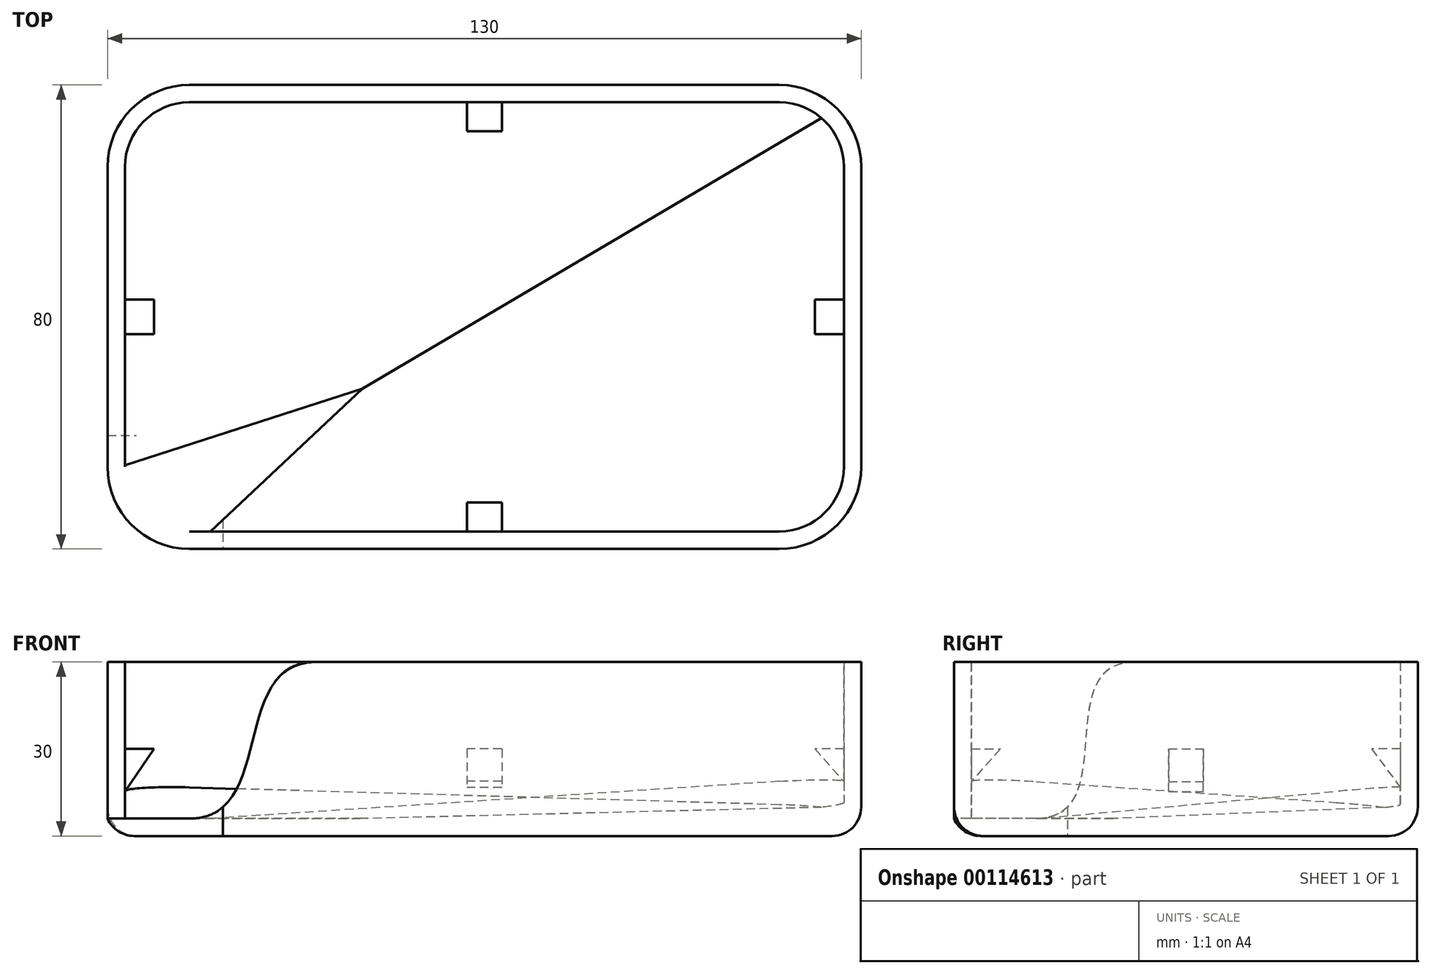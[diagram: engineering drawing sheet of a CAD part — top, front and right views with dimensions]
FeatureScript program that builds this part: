
annotation { "Feature Type Name" : "Feature", "Feature Type Description" : "" }
export const myFeature = defineFeature(function(context is Context, id is Id, definition is map)
    precondition{}
    {
        {
            var Q0;
            Q0=qCreatedBy(makeId("Top.planeOp"),FACE);
            var sketch = newSketch(context, id + "F0", { "sketchPlane" : qUnion([Q0])});
            skLineSegment(sketch, "E0.bottom", {"start": v(65, -40) * mm, "end": v(50.86, -40) * mm, "construction": true});
            skLineSegment(sketch, "E0.top", {"start": v(65, 40) * mm, "end": v(50.86, 40) * mm, "construction": true});
            skLineSegment(sketch, "E0.left", {"start": v(65, -40) * mm, "end": v(65, -25.86) * mm, "construction": true});
            skLineSegment(sketch, "E0.right", {"start": v(-65, -40) * mm, "end": v(-65, -25.86) * mm, "construction": true});
            skPoint(sketch, "E0.middle", {"position": v(0, 0) * mm});
            skArc(sketch, "E1", {"start": v(-50.86, 40) * mm, "mid": v(-60.86, 35.86) * mm, "end": v(-65, 25.86) * mm});
            skArc(sketch, "E2", {"start": v(-65, -25.86) * mm, "mid": v(-60.86, -35.86) * mm, "end": v(-50.86, -40) * mm});
            skArc(sketch, "E3", {"start": v(65, 25.86) * mm, "mid": v(60.86, 35.86) * mm, "end": v(50.86, 40) * mm});
            skArc(sketch, "E4", {"start": v(50.86, -40) * mm, "mid": v(60.86, -35.86) * mm, "end": v(65, -25.86) * mm});
            skLineSegment(sketch, "E5", {"start": v(65, 40) * mm, "end": v(50.86, 25.86) * mm, "construction": true});
            skLineSegment(sketch, "E6", {"start": v(-65, 40) * mm, "end": v(-50.86, 25.86) * mm, "construction": true});
            skLineSegment(sketch, "E7", {"start": v(-50.86, -25.86) * mm, "end": v(-65, -40) * mm, "construction": true});
            skLineSegment(sketch, "E8", {"start": v(50.86, -25.86) * mm, "end": v(65, -40) * mm, "construction": true});
            skLineSegment(sketch, "E9", {"start": v(-50.86, 40) * mm, "end": v(-65, 40) * mm, "construction": true});
            skLineSegment(sketch, "E10", {"start": v(-65, 25.86) * mm, "end": v(-65, 40) * mm, "construction": true});
            skLineSegment(sketch, "E11", {"start": v(-65, -25.86) * mm, "end": v(-65, 25.86) * mm});
            skLineSegment(sketch, "E12", {"start": v(-50.86, -40) * mm, "end": v(-65, -40) * mm, "construction": true});
            skLineSegment(sketch, "E13", {"start": v(50.86, -40) * mm, "end": v(-50.86, -40) * mm});
            skLineSegment(sketch, "E14", {"start": v(65, -25.86) * mm, "end": v(65, 25.86) * mm});
            skLineSegment(sketch, "E15", {"start": v(65, 25.86) * mm, "end": v(65, 40) * mm, "construction": true});
            skLineSegment(sketch, "E16", {"start": v(50.86, 40) * mm, "end": v(-50.86, 40) * mm});
            skLineSegment(sketch, "E17", {"start": v(-60.86, 35.86) * mm, "end": v(60.86, -35.86) * mm, "construction": true});
            skLineSegment(sketch, "E18", {"start": v(60.86, 35.86) * mm, "end": v(-60.86, -35.86) * mm, "construction": true});
            skLineSegment(sketch, "E19", {"start": v(39.73, 71.72) * mm, "end": v(81.99, 0) * mm, "construction": true});
            skLineSegment(sketch, "E20", {"start": v(-65, -25.86) * mm, "end": v(-50.86, -40) * mm, "construction": true});
            skSolve(sketch);
        }
        {
            var Q0;
            Q0 = qSketchRegion(id + "F0", true);
            extrude(context, id + "F1", {"entities" : qUnion([Q0]), "depth" : 30 * mm});
        }
        {
            var Q0;
            Q0=makeQuery(id+"F1.opExtrude","CAP_FACE",FACE,{"disambiguationData":[OSD([sQuery(id+"F0.wireOp",EDGE,"E1"),sQuery(id+"F0.wireOp",EDGE,"E2"),sQuery(id+"F0.wireOp",EDGE,"E3"),sQuery(id+"F0.wireOp",EDGE,"E4"),sQuery(id+"F0.wireOp",EDGE,"E11"),sQuery(id+"F0.wireOp",EDGE,"E13"),sQuery(id+"F0.wireOp",EDGE,"E14"),sQuery(id+"F0.wireOp",EDGE,"E16")])],"isStart":false});
            shell(context, id + "F2", {"entities" : qUnion([Q0]), "thickness" : 3 * mm});
        }
        {
            var Q0;
            Q0=sQuery(id+"F0.wireOp",EDGE,"E19");
            cPlane(context, id + "F3", {"entities" : qUnion([Q0]), "cplaneType" : CPlaneType.LINE_ANGLE, "offset" : 25 * mm, "angle" : 90 * degree, "width" : 150 * mm, "height" : 150 * mm});
        }
        {
            var Q0;
            Q0=qCreatedBy(id+"F3.planeOp",FACE);
            var sketch = newSketch(context, id + "F4", { "sketchPlane" : qUnion([Q0])});
            skLineSegment(sketch, "E21.0", {"start": v(-10.72, 0) * mm, "end": v(8.65, 0) * mm, "construction": true});
            skLineSegment(sketch, "E22", {"start": v(0, 0) * mm, "end": v(75, 0) * mm});
            skPoint(sketch, "E22.endSnap0", {"position": v(-1.04, 0) * mm});
            skLineSegment(sketch, "E23", {"start": v(75, 0) * mm, "end": v(75, 12) * mm});
            skLineSegment(sketch, "E24", {"start": v(0, 0) * mm, "end": v(0, 5) * mm, "construction": true});
            skLineSegment(sketch, "E25", {"start": v(75, 12) * mm, "end": v(0, 5) * mm});
            skLineSegment(sketch, "E26.MirrorCS", {"start": v(0, 0) * mm, "end": v(-75, 0) * mm});
            skLineSegment(sketch, "E27.MirrorCS", {"start": v(-75, 0) * mm, "end": v(-75, 12) * mm});
            skLineSegment(sketch, "E28.MirrorCS", {"start": v(-75, 12) * mm, "end": v(0, 5) * mm});
            skSolve(sketch);
        }
        {
            var Q0;
            Q0 = qSketchRegion(id + "F4", true);
            extrude(context, id + "F5", {"entities" : qUnion([Q0]), "operationType" : NewBodyOperationType.ADD, "oppositeDirection" : true, "depth" : 140 * mm, "hasDraft" : true, "draftAngle" : 1.2 * degree, "draftPullDirection" : true});
        }
        {
            var Q0;
            Q0=qCreatedBy(makeId("Top.planeOp"),FACE);
            var sketch = newSketch(context, id + "F6", { "sketchPlane" : qUnion([Q0])});
            skArc(sketch, "E29.0", {"start": v(-50.86, 40) * mm, "mid": v(-60.86, 35.86) * mm, "end": v(-65, 25.86) * mm});
            skLineSegment(sketch, "E29.1", {"start": v(-65, -25.86) * mm, "end": v(-65, 25.86) * mm});
            skArc(sketch, "E29.2", {"start": v(-65, -25.86) * mm, "mid": v(-60.86, -35.86) * mm, "end": v(-50.86, -40) * mm});
            skLineSegment(sketch, "E29.3", {"start": v(50.86, -40) * mm, "end": v(-50.86, -40) * mm});
            skArc(sketch, "E29.4", {"start": v(50.86, -40) * mm, "mid": v(60.86, -35.86) * mm, "end": v(65, -25.86) * mm});
            skLineSegment(sketch, "E29.5", {"start": v(65, -25.86) * mm, "end": v(65, 25.86) * mm});
            skArc(sketch, "E29.6", {"start": v(65, 25.86) * mm, "mid": v(60.86, 35.86) * mm, "end": v(50.86, 40) * mm});
            skLineSegment(sketch, "E29.7", {"start": v(50.86, 40) * mm, "end": v(-50.86, 40) * mm});
            skLineSegment(sketch, "E30", {"start": v(-101.68, 119.74) * mm, "end": v(120.2, 119.74) * mm});
            skLineSegment(sketch, "E31", {"start": v(120.2, 119.74) * mm, "end": v(120.2, -100.68) * mm});
            skLineSegment(sketch, "E32", {"start": v(120.2, -100.68) * mm, "end": v(-101.68, -100.68) * mm});
            skLineSegment(sketch, "E33", {"start": v(-101.68, -100.68) * mm, "end": v(-101.68, 119.74) * mm});
            skSolve(sketch);
        }
        {
            var Q0;
            Q0 = qSketchRegion(id + "F6", true);
            extrude(context, id + "F7", {"entities" : qUnion([Q0]), "operationType" : NewBodyOperationType.REMOVE, "depth" : 25 * mm});
        }
        {
            var Q0;
            {var subQ2=sQuery(id+"F0.wireOp",EDGE,"E13");var subQ10=makeQuery(id+"F1.opExtrude","SWEPT_FACE",FACE,{"disambiguationData":[OSD([subQ2])]});Q0=makeQuery(id+"F7.boolean.opBoolean","MERGE",FACE,{"derivedFrom":[makeQuery(id+"F5.boolean.opBoolean","SPLIT",FACE,{"disambiguationData":[TD([makeQuery(id+"F5.opExtrude","SWEPT_FACE",FACE,{"disambiguationData":[OSD([sQuery(id+"F4.wireOp",EDGE,"E22"),sQuery(id+"F4.wireOp",EDGE,"E26.MirrorCS")])]})])],"derivedFrom":subQ10}),makeQuery(id+"F5.boolean.opBoolean","SPLIT",FACE,{"disambiguationData":[TD([makeQuery(id+"F5.opExtrude","SWEPT_FACE",FACE,{"disambiguationData":[OSD([sQuery(id+"F4.wireOp",EDGE,"E28.MirrorCS")])]})])],"derivedFrom":subQ10}),makeQuery(id+"F7.opExtrude","SWEPT_FACE",FACE,{"disambiguationData":[OSD([sQuery(id+"F6.wireOp",EDGE,"E29.3")])]})]});}
            var sketch = newSketch(context, id + "F8", { "sketchPlane" : qUnion([Q0])});
            skLineSegment(sketch, "E34.0", {"start": v(-47.23, 3) * mm, "end": v(-50.86, 3) * mm, "construction": true});
            skFitSpline(sketch, "E35", {"points": [v(-50.86, 3) * mm, v(-29.05, 30) * mm], "startDerivative": vector(45, 0) * mm, "endDerivative": vector(45, 0) * mm});
            skLineSegment(sketch, "E36", {"start": v(-35.86, 3) * mm, "end": v(-50.86, 3) * mm, "construction": true});
            skLineSegment(sketch, "E37", {"start": v(-29.05, 30) * mm, "end": v(-44.05, 30) * mm, "construction": true});
            skLineSegment(sketch, "E38.0", {"start": v(50.86, 30) * mm, "end": v(-50.86, 30) * mm});
            skLineSegment(sketch, "E39", {"start": v(-50.86, 30) * mm, "end": v(-50.86, 3) * mm});
            skSolve(sketch);
        }
        {
            var Q0;
            Q0 = qSketchRegion(id + "F8", true);
            var Q1;
            Q1=makeQuery(id+"F2.opShell","OFFSET_FACE",FACE,{"disambiguationData":[OSD([sQuery(id+"F0.wireOp",EDGE,"E13")])]});
            extrude(context, id + "F9", {"entities" : qUnion([Q0]), "operationType" : NewBodyOperationType.REMOVE, "endBound" : BoundingType.UP_TO_SURFACE, "oppositeDirection" : true, "endBoundEntityFace" : qUnion([Q1]), "depth" : 25 * mm});
        }
        {
            var Q0;
            {var subQ5=sQuery(id+"F0.wireOp",EDGE,"E11");var subQ10=makeQuery(id+"F1.opExtrude","SWEPT_FACE",FACE,{"disambiguationData":[OSD([subQ5])]});Q0=makeQuery(id+"F7.boolean.opBoolean","MERGE",FACE,{"derivedFrom":[makeQuery(id+"F5.boolean.opBoolean","SPLIT",FACE,{"disambiguationData":[TD([makeQuery(id+"F5.opExtrude","SWEPT_FACE",FACE,{"disambiguationData":[OSD([sQuery(id+"F4.wireOp",EDGE,"E22"),sQuery(id+"F4.wireOp",EDGE,"E26.MirrorCS")])]})])],"derivedFrom":subQ10}),makeQuery(id+"F5.boolean.opBoolean","SPLIT",FACE,{"disambiguationData":[TD([makeQuery(id+"F5.opExtrude","SWEPT_FACE",FACE,{"disambiguationData":[OSD([sQuery(id+"F4.wireOp",EDGE,"E25")])]})])],"derivedFrom":subQ10}),makeQuery(id+"F7.opExtrude","SWEPT_FACE",FACE,{"disambiguationData":[OSD([sQuery(id+"F6.wireOp",EDGE,"E29.1")])]})]});}
            var sketch = newSketch(context, id + "F10", { "sketchPlane" : qUnion([Q0])});
            skLineSegment(sketch, "E40.0", {"start": v(25.86, 3) * mm, "end": v(25.55, 3) * mm, "construction": true});
            skLineSegment(sketch, "E41.0", {"start": v(25.86, 30) * mm, "end": v(-25.86, 30) * mm});
            skFitSpline(sketch, "E42", {"points": [v(8.75, 30) * mm, v(25.86, 3) * mm], "startDerivative": vector(45, 0) * mm, "endDerivative": vector(45, 0) * mm});
            skLineSegment(sketch, "E43", {"start": v(8.75, 30) * mm, "end": v(23.75, 30) * mm, "construction": true});
            skLineSegment(sketch, "E44", {"start": v(25.86, 3) * mm, "end": v(10.86, 3) * mm, "construction": true});
            skLineSegment(sketch, "E45", {"start": v(25.86, 30) * mm, "end": v(25.86, 3) * mm});
            skSolve(sketch);
        }
        {
            var Q0;
            Q0 = qSketchRegion(id + "F10", true);
            var Q1;
            Q1=makeQuery(id+"F2.opShell","OFFSET_FACE",FACE,{"disambiguationData":[OSD([sQuery(id+"F0.wireOp",EDGE,"E11")])]});
            extrude(context, id + "F11", {"entities" : qUnion([Q0]), "operationType" : NewBodyOperationType.REMOVE, "endBound" : BoundingType.UP_TO_SURFACE, "oppositeDirection" : true, "endBoundEntityFace" : qUnion([Q1]), "depth" : 25 * mm});
        }
        {
            var Q0;
            Q0=makeQuery(id+"F2.opShell","OFFSET_FACE",FACE,{"disambiguationData":[OSD([sQuery(id+"F0.wireOp",EDGE,"E1"),sQuery(id+"F0.wireOp",EDGE,"E2"),sQuery(id+"F0.wireOp",EDGE,"E3"),sQuery(id+"F0.wireOp",EDGE,"E4"),sQuery(id+"F0.wireOp",EDGE,"E11"),sQuery(id+"F0.wireOp",EDGE,"E13"),sQuery(id+"F0.wireOp",EDGE,"E14"),sQuery(id+"F0.wireOp",EDGE,"E16")])]});
            var sketch = newSketch(context, id + "F12", { "sketchPlane" : qUnion([Q0])});
            skArc(sketch, "E46.0", {"start": v(-65, -25.86) * mm, "mid": v(-60.86, -35.86) * mm, "end": v(-50.86, -40) * mm});
            skArc(sketch, "E46.1", {"start": v(-62, -25.86) * mm, "mid": v(-58.74, -33.74) * mm, "end": v(-50.86, -37) * mm});
            skLineSegment(sketch, "E46.2", {"start": v(-62, -25.86) * mm, "end": v(-65, -25.86) * mm});
            skLineSegment(sketch, "E46.3", {"start": v(-50.86, -37) * mm, "end": v(-50.86, -40) * mm});
            skSolve(sketch);
        }
        {
            var Q0;
            Q0 = qSketchRegion(id + "F12", true);
            var Q1;
            {var subQ0=sQuery(id+"F0.wireOp",EDGE,"E14");var subQ1=sQuery(id+"F0.wireOp",EDGE,"E11");var subQ2=sQuery(id+"F0.wireOp",EDGE,"E3");var subQ3=sQuery(id+"F0.wireOp",EDGE,"E16");var subQ4=sQuery(id+"F0.wireOp",EDGE,"E4");var subQ5=sQuery(id+"F0.wireOp",EDGE,"E13");var subQ6=sQuery(id+"F0.wireOp",EDGE,"E1");Q1=makeQuery(id+"F11.boolean.opBoolean","SPLIT",FACE,{"disambiguationData":[TD([makeQuery(id+"F1.opExtrude","SWEPT_FACE",FACE,{"disambiguationData":[OSD([subQ6])]})])],"derivedFrom":makeQuery(id+"F1.opExtrude","CAP_FACE",FACE,{"disambiguationData":[OSD([subQ6,sQuery(id+"F0.wireOp",EDGE,"E2"),subQ2,subQ4,subQ1,subQ5,subQ0,subQ3])],"isStart":false})});}
            extrude(context, id + "F13", {"entities" : qUnion([Q0]), "operationType" : NewBodyOperationType.REMOVE, "endBound" : BoundingType.UP_TO_SURFACE, "endBoundEntityFace" : qUnion([Q1]), "depth" : 25 * mm});
        }
        {
            var Q0;
            Q0=makeQuery(id+"F1.opExtrude","CAP_FACE",FACE,{"disambiguationData":[OSD([sQuery(id+"F0.wireOp",EDGE,"E1"),sQuery(id+"F0.wireOp",EDGE,"E2"),sQuery(id+"F0.wireOp",EDGE,"E3"),sQuery(id+"F0.wireOp",EDGE,"E4"),sQuery(id+"F0.wireOp",EDGE,"E11"),sQuery(id+"F0.wireOp",EDGE,"E13"),sQuery(id+"F0.wireOp",EDGE,"E14"),sQuery(id+"F0.wireOp",EDGE,"E16")])],"isStart":true});
            fillet(context, id + "F14", {"entities" : qUnion([Q0]), "radius" : 5 * mm, "tangentPropagation" : true, "allowEdgeOverflow" : false});
        }
        {
            var Q0;
            Q0=qCreatedBy(makeId("Front.planeOp"),FACE);
            var sketch = newSketch(context, id + "F15", { "sketchPlane" : qUnion([Q0])});
            skFitSpline(sketch, "E47.0", {"points": [v(-62, 3.12) * mm, v(-62, 12.08) * mm, v(-62, 21.04) * mm, v(-62, 30) * mm]});
            skLineSegment(sketch, "E48.0", {"start": v(62, 30) * mm, "end": v(62, 9.38) * mm});
            skLineSegment(sketch, "E49", {"start": v(-62, 30) * mm, "end": v(-62, 0) * mm, "construction": true});
            skLineSegment(sketch, "E50", {"start": v(62, 30) * mm, "end": v(62, 0) * mm, "construction": true});
            skLineSegment(sketch, "E51", {"start": v(-62, 15) * mm, "end": v(-57, 15) * mm});
            skLineSegment(sketch, "E52", {"start": v(62, 15) * mm, "end": v(57, 15) * mm});
            skPoint(sketch, "E52.endSnap0", {"position": v(62, 15) * mm});
            skEllipticalArc(sketch, "E53.0", {});
            skEllipticalArc(sketch, "E54.0", {});
            skLineSegment(sketch, "E55", {"start": v(-57, 15) * mm, "end": v(-62, 7.68) * mm});
            skLineSegment(sketch, "E56", {"start": v(57, 15) * mm, "end": v(62, 9.38) * mm});
            const initialGuessF15  = {"E53.0": [-0.050857864376269046, 0.0073572243298795775, 0.9995651955649583, -0.029485925713581156, 0.011146942206523262, 0.0010145309923370737, 1.5734811282030245, 3.1442774549979204], "E54.0": [0.050857864376269046, 0.008648581469915026, -0.9978405935118139, -0.0656821889098638, 0.011166131468866098, 0.00077530749382443, 3.137022248751718, 4.707818575546617]};
            skSetInitialGuess(sketch, initialGuessF15);
            skSolve(sketch);
        }
        {
            var Q0;
            Q0 = qSketchRegion(id + "F15", true);
            extrude(context, id + "F16", {"entities" : qUnion([Q0]), "operationType" : NewBodyOperationType.ADD, "depth" : 6 * mm, "symmetric" : true});
        }
        {
            var Q0;
            Q0=qCreatedBy(makeId("Right.planeOp"),FACE);
            var sketch = newSketch(context, id + "F17", { "sketchPlane" : qUnion([Q0])});
            skLineSegment(sketch, "E57.0", {"start": v(-37, 30) * mm, "end": v(-37, 9.43) * mm});
            skLineSegment(sketch, "E58.0", {"start": v(37, 30) * mm, "end": v(37, 5.4) * mm});
            skEllipticalArc(sketch, "E59.0", {});
            skEllipticalArc(sketch, "E60.0", {});
            skLineSegment(sketch, "E61", {"start": v(-37, 30) * mm, "end": v(-37, 0) * mm, "construction": true});
            skLineSegment(sketch, "E62", {"start": v(37, 30) * mm, "end": v(37, 0) * mm, "construction": true});
            skLineSegment(sketch, "E63", {"start": v(-37, 15) * mm, "end": v(-32, 15) * mm});
            skLineSegment(sketch, "E64", {"start": v(37, 15) * mm, "end": v(32, 15) * mm});
            skLineSegment(sketch, "E65", {"start": v(32, 15) * mm, "end": v(37, 8.37) * mm});
            skLineSegment(sketch, "E66", {"start": v(-32, 15) * mm, "end": v(-37, 9.43) * mm});
            const initialGuessF17  = {"E59.0": [0.025857864376269038, 0.0073572243298795775, -0.9958697267958021, -0.09079365204492344, 0.011188307410707204, 0.00032460895473833645, 3.1389475173384467, 4.709743844133345], "E60.0": [-0.025857864376269038, 0.008648581469915026, 0.9975567231146678, -0.06986117783666451, 0.011169309233015658, 0.0007280967979968894, 1.5753615087569885, 3.1461578355518856]};
            skSetInitialGuess(sketch, initialGuessF17);
            skSolve(sketch);
        }
        {
            var Q0;
            Q0 = qSketchRegion(id + "F17", true);
            extrude(context, id + "F18", {"entities" : qUnion([Q0]), "operationType" : NewBodyOperationType.ADD, "depth" : 6 * mm, "symmetric" : true});
        }
    });
